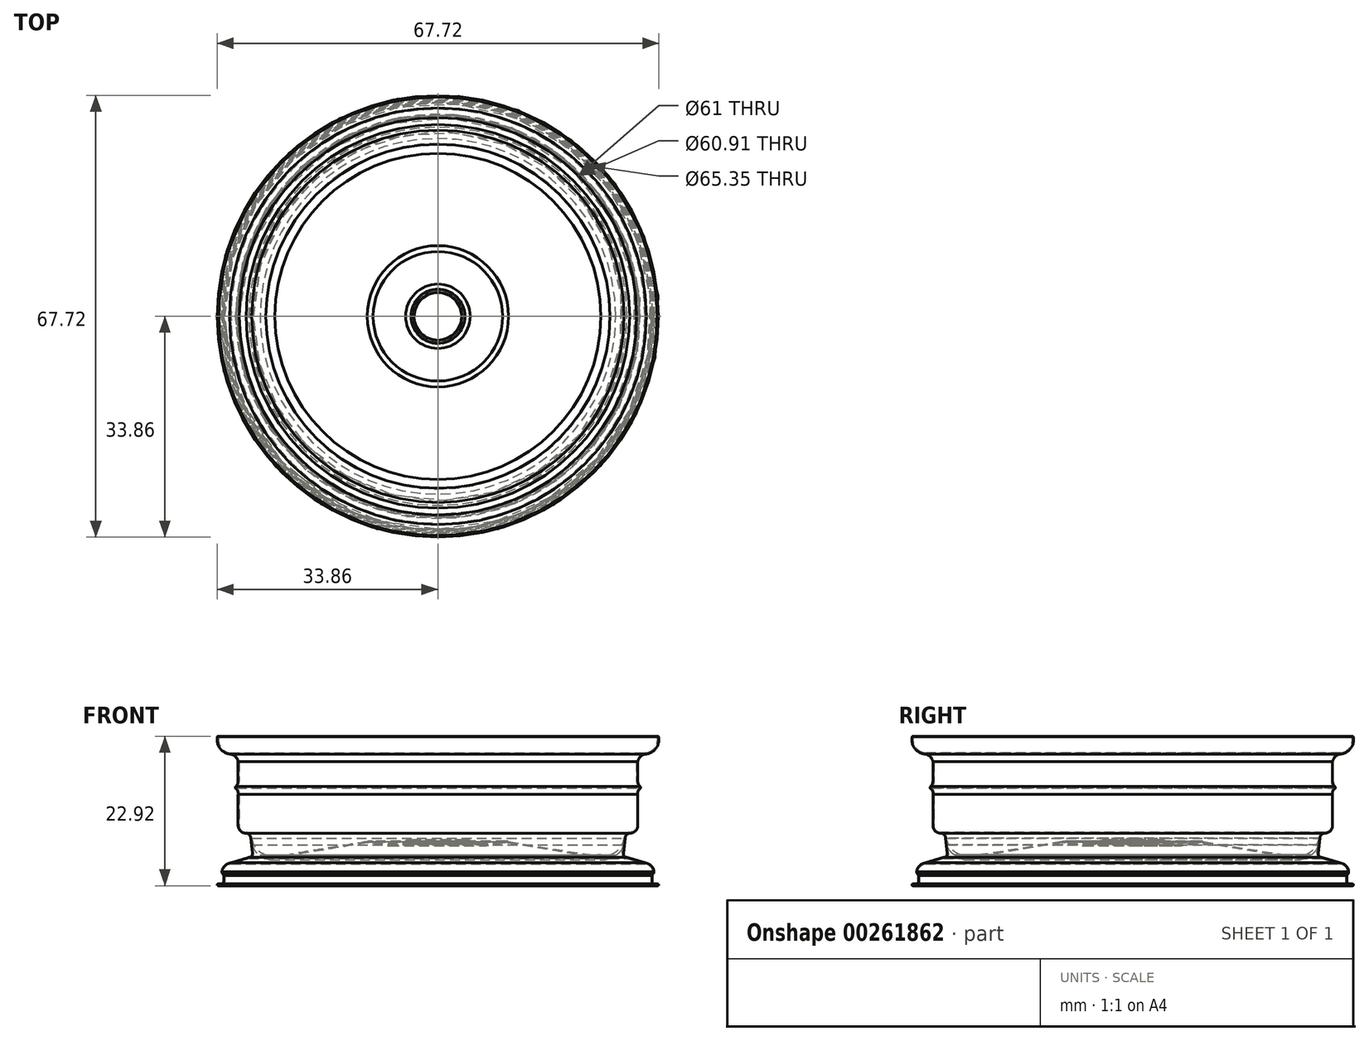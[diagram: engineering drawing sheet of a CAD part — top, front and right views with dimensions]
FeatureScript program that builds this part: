
annotation { "Feature Type Name" : "Feature", "Feature Type Description" : "" }
export const myFeature = defineFeature(function(context is Context, id is Id, definition is map)
    precondition{}
    {
        {
            var Q0;
            Q0=qCreatedBy(makeId("Top.planeOp"),FACE);
            var sketch = newSketch(context, id + "F0", { "sketchPlane" : qUnion([Q0])});
            skCircle(sketch, "E0", {"center": v(0, 0) * mm, "radius": 28.2 * mm});
            skSolve(sketch);
        }
        {
            var Q0;
            Q0=qCreatedBy(makeId("Right.planeOp"),FACE);
            var sketch = newSketch(context, id + "F1", { "sketchPlane" : qUnion([Q0])});
            skArc(sketch, "E1", {"start": v(-33.8, 16.54) * mm, "mid": v(-33.45, 14.82) * mm, "end": v(-31.95, 13.9) * mm});
            skArc(sketch, "E2", {"start": v(-30.63, 12.75) * mm, "mid": v(-31.1, 13.55) * mm, "end": v(-31.95, 13.9) * mm});
            skLineSegment(sketch, "E3", {"start": v(-30.63, 12.75) * mm, "end": v(-30.63, 9.8) * mm});
            skArc(sketch, "E4", {"start": v(-30.97, 8.93) * mm, "mid": v(-30.72, 9.33) * mm, "end": v(-30.63, 9.8) * mm});
            skArc(sketch, "E5", {"start": v(-30.97, 8.93) * mm, "mid": v(-31.06, 8.75) * mm, "end": v(-30.97, 8.57) * mm});
            skArc(sketch, "E6", {"start": v(-30.63, 7.73) * mm, "mid": v(-30.68, 8.2) * mm, "end": v(-30.97, 8.57) * mm});
            skLineSegment(sketch, "E7", {"start": v(-30.63, 7.73) * mm, "end": v(-30.63, 2.93) * mm});
            skArc(sketch, "E8", {"start": v(-30.63, 2.93) * mm, "mid": v(-30.26, 2.08) * mm, "end": v(-29.39, 1.76) * mm});
            skArc(sketch, "E9", {"start": v(-28.69, 1.01) * mm, "mid": v(-28.91, 1.5) * mm, "end": v(-29.39, 1.76) * mm});
            skLineSegment(sketch, "E10", {"start": v(-28.69, 1.01) * mm, "end": v(-28.43, -1.29) * mm});
            skArc(sketch, "E11", {"start": v(-28.99, -1.96) * mm, "mid": v(-28.57, -1.74) * mm, "end": v(-28.43, -1.29) * mm});
            skArc(sketch, "E12", {"start": v(-31.75, -2.79) * mm, "mid": v(-32.67, -3.21) * mm, "end": v(-33.12, -4.13) * mm});
            skArc(sketch, "E13", {"start": v(-33.12, -4.13) * mm, "mid": v(-33.06, -4.38) * mm, "end": v(-32.9, -4.59) * mm});
            skArc(sketch, "E14", {"start": v(-32.85, -4.71) * mm, "mid": v(-32.86, -4.64) * mm, "end": v(-32.9, -4.59) * mm});
            skLineSegment(sketch, "E15", {"start": v(-32.85, -4.71) * mm, "end": v(-32.85, -5.65) * mm});
            skArc(sketch, "E16", {"start": v(-33.25, -6.06) * mm, "mid": v(-32.96, -5.94) * mm, "end": v(-32.85, -5.65) * mm});
            skArc(sketch, "E17", {"start": v(-33.6, -6.06) * mm, "mid": v(-33.43, -6.07) * mm, "end": v(-33.25, -6.06) * mm});
            skArc(sketch, "E18", {"start": v(-33.6, -6.06) * mm, "mid": v(-33.78, -6.05) * mm, "end": v(-33.8, -6.22) * mm});
            skArc(sketch, "E19", {"start": v(-33.61, 16.54) * mm, "mid": v(-33.71, 16.63) * mm, "end": v(-33.8, 16.54) * mm});
            skArc(sketch, "E20", {"start": v(-33.61, 16.54) * mm, "mid": v(-33.3, 14.95) * mm, "end": v(-31.94, 14.06) * mm});
            skArc(sketch, "E21", {"start": v(-30.45, 12.72) * mm, "mid": v(-30.98, 13.63) * mm, "end": v(-31.94, 14.06) * mm});
            skLineSegment(sketch, "E22", {"start": v(-30.45, 12.72) * mm, "end": v(-30.45, 9.74) * mm});
            skArc(sketch, "E23", {"start": v(-30.83, 8.87) * mm, "mid": v(-30.55, 9.26) * mm, "end": v(-30.45, 9.74) * mm});
            skArc(sketch, "E24", {"start": v(-30.83, 8.87) * mm, "mid": v(-30.9, 8.76) * mm, "end": v(-30.83, 8.65) * mm});
            skArc(sketch, "E25", {"start": v(-30.5, 7.72) * mm, "mid": v(-30.53, 8.24) * mm, "end": v(-30.83, 8.65) * mm});
            skLineSegment(sketch, "E26", {"start": v(-30.5, 7.72) * mm, "end": v(-30.5, 2.93) * mm});
            skArc(sketch, "E27", {"start": v(-30.5, 2.93) * mm, "mid": v(-30.17, 2.18) * mm, "end": v(-29.4, 1.9) * mm});
            skArc(sketch, "E28", {"start": v(-28.54, 1.01) * mm, "mid": v(-28.82, 1.6) * mm, "end": v(-29.4, 1.9) * mm});
            skArc(sketch, "E29", {"start": v(-28.96, -2.11) * mm, "mid": v(-28.44, -1.86) * mm, "end": v(-28.27, -1.3) * mm});
            skArc(sketch, "E30", {"start": v(-31.74, -2.94) * mm, "mid": v(-32.56, -3.32) * mm, "end": v(-32.95, -4.13) * mm});
            skArc(sketch, "E31", {"start": v(-32.95, -4.13) * mm, "mid": v(-32.91, -4.34) * mm, "end": v(-32.77, -4.5) * mm});
            skArc(sketch, "E32", {"start": v(-32.67, -4.72) * mm, "mid": v(-32.7, -4.6) * mm, "end": v(-32.77, -4.5) * mm});
            skLineSegment(sketch, "E33", {"start": v(-32.67, -4.72) * mm, "end": v(-32.67, -5.68) * mm});
            skArc(sketch, "E34", {"start": v(-33.23, -6.2) * mm, "mid": v(-32.84, -6.06) * mm, "end": v(-32.67, -5.68) * mm});
            skLineSegment(sketch, "E35", {"start": v(-33.23, -6.2) * mm, "end": v(-33.62, -6.2) * mm});
            skArc(sketch, "E36", {"start": v(-33.8, -6.22) * mm, "mid": v(-33.7, -6.29) * mm, "end": v(-33.62, -6.2) * mm});
            skLineSegment(sketch, "E37", {"start": v(-28.27, -1.3) * mm, "end": v(-28.41, 0) * mm});
            skArc(sketch, "E38", {"start": v(-28.41, 0) * mm, "mid": v(-28.04, -0.95) * mm, "end": v(-27.25, -1.58) * mm});
            skArc(sketch, "E39", {"start": v(-26.48, -1.84) * mm, "mid": v(-25.75, -2.29) * mm, "end": v(-25, -1.84) * mm});
            skArc(sketch, "E40", {"start": v(-27.25, -1.58) * mm, "mid": v(-26.88, -1.75) * mm, "end": v(-26.48, -1.84) * mm});
            skArc(sketch, "E41", {"start": v(-25, -1.84) * mm, "mid": v(-23.59, -1.75) * mm, "end": v(-22.18, -1.57) * mm});
            skLineSegment(sketch, "E42", {"start": v(-22.18, -1.57) * mm, "end": v(-10.71, 0.32) * mm});
            skArc(sketch, "E43", {"start": v(-9.99, 0.32) * mm, "mid": v(-10.35, 0.35) * mm, "end": v(-10.71, 0.32) * mm});
            skArc(sketch, "E44", {"start": v(-9.99, 0.32) * mm, "mid": v(-7.46, -0.13) * mm, "end": v(-4.94, 0.32) * mm});
            skArc(sketch, "E45", {"start": v(-4.24, 0.48) * mm, "mid": v(-4.6, 0.46) * mm, "end": v(-4.94, 0.32) * mm});
            skArc(sketch, "E46", {"start": v(-3.98, 0.32) * mm, "mid": v(-4.08, 0.44) * mm, "end": v(-4.24, 0.48) * mm});
            skArc(sketch, "E47", {"start": v(-3.98, 0.32) * mm, "mid": v(-3.82, 0.13) * mm, "end": v(-3.66, 0.32) * mm});
            skArc(sketch, "E48", {"start": v(-3.66, 0.32) * mm, "mid": v(-3.82, 0.61) * mm, "end": v(-4.13, 0.73) * mm});
            skArc(sketch, "E49", {"start": v(-4.13, 0.73) * mm, "mid": v(-4.55, 0.72) * mm, "end": v(-4.94, 0.58) * mm});
            skArc(sketch, "E50", {"start": v(-9.93, 0.48) * mm, "mid": v(-7.42, 0.05) * mm, "end": v(-4.94, 0.58) * mm});
            skArc(sketch, "E51", {"start": v(-9.93, 0.48) * mm, "mid": v(-10.38, 0.54) * mm, "end": v(-10.83, 0.48) * mm});
            skLineSegment(sketch, "E52", {"start": v(-10.83, 0.48) * mm, "end": v(-22.21, -1.4) * mm});
            skArc(sketch, "E53", {"start": v(-25, -1.57) * mm, "mid": v(-23.6, -1.55) * mm, "end": v(-22.21, -1.4) * mm});
            skArc(sketch, "E54", {"start": v(-26.37, -1.57) * mm, "mid": v(-25.68, -1.98) * mm, "end": v(-25, -1.57) * mm});
            skArc(sketch, "E55", {"start": v(-28.54, 1.01) * mm, "mid": v(-27.83, -0.59) * mm, "end": v(-26.37, -1.57) * mm});
            skLineSegment(sketch, "E56", {"start": v(-28.99, -1.96) * mm, "end": v(-31.75, -2.79) * mm});
            skLineSegment(sketch, "E57", {"start": v(-28.96, -2.11) * mm, "end": v(-31.74, -2.94) * mm});
            skSolve(sketch);
        }
        {
            var Q0;
            Q0 = qSketchRegion(id + "F1", true);
            var Q1;
            Q1=sQuery(id+"F0.wireOp",EDGE,"E0");
            revolve(context, id + "F2", {"entities" : qUnion([Q0]), "axis" : qUnion([Q1]), "revolveType" : RevolveType.FULL});
        }
    });
